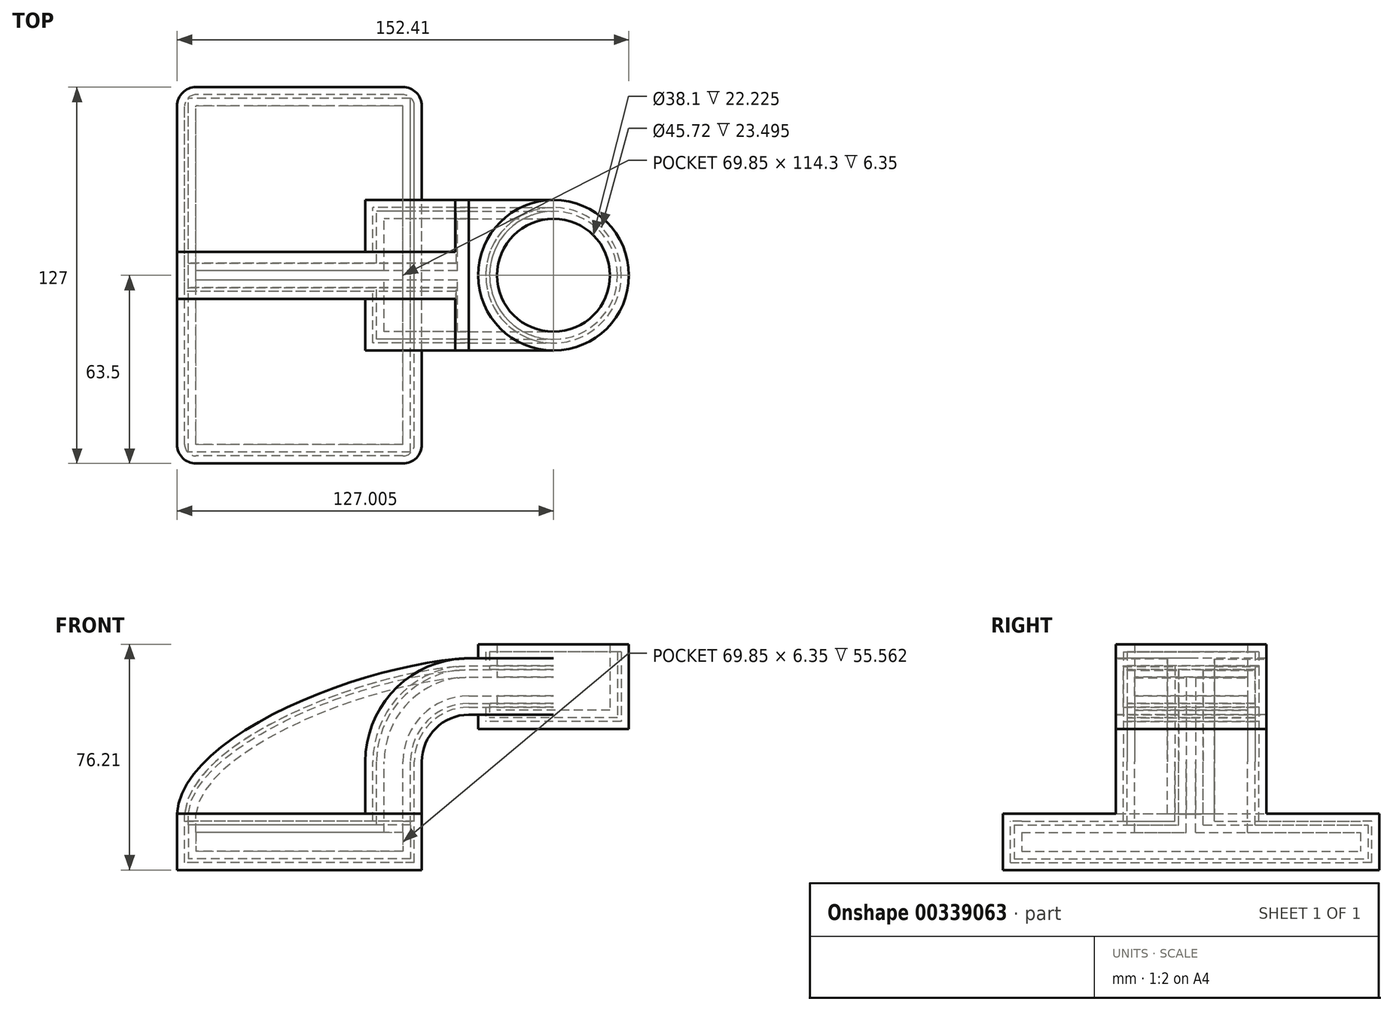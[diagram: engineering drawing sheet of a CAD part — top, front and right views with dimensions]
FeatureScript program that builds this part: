
annotation { "Feature Type Name" : "Feature", "Feature Type Description" : "" }
export const myFeature = defineFeature(function(context is Context, id is Id, definition is map)
    precondition{}
    {
        {
            var Q0;
            Q0=qCreatedBy(makeId("Front.planeOp"),FACE);
            var sketch = newSketch(context, id + "F0", { "sketchPlane" : qUnion([Q0])});
            skLineSegment(sketch, "E0.bottom", {"start": v(41.28, -9.52) * mm, "end": v(-41.28, -9.53) * mm});
            skLineSegment(sketch, "E0.top", {"start": v(41.28, 9.53) * mm, "end": v(-41.28, 9.53) * mm});
            skLineSegment(sketch, "E0.left", {"start": v(41.28, -9.52) * mm, "end": v(41.28, 9.53) * mm});
            skLineSegment(sketch, "E0.right", {"start": v(-41.28, -9.53) * mm, "end": v(-41.28, 9.53) * mm});
            skPoint(sketch, "E0.middle", {"position": v(0, 0) * mm});
            skLineSegment(sketch, "E1.bottom", {"start": v(111.13, 38.1) * mm, "end": v(60.33, 38.1) * mm});
            skLineSegment(sketch, "E1.top", {"start": v(111.13, 66.68) * mm, "end": v(60.33, 66.68) * mm});
            skLineSegment(sketch, "E1.left", {"start": v(111.13, 38.1) * mm, "end": v(111.13, 66.68) * mm});
            skLineSegment(sketch, "E1.right", {"start": v(60.33, 38.1) * mm, "end": v(60.33, 66.68) * mm});
            skPoint(sketch, "E1.middle", {"position": v(85.73, 52.39) * mm});
            skLineSegment(sketch, "E2", {"start": v(41.28, 9.53) * mm, "end": v(41.28, 27) * mm});
            skArc(sketch, "E3", {"start": v(41.27, 27) * mm, "mid": v(45.92, 38.23) * mm, "end": v(57.15, 42.88) * mm});
            skLineSegment(sketch, "E4", {"start": v(57.15, 42.88) * mm, "end": v(85.72, 42.88) * mm});
            skArc(sketch, "E5.0", {"start": v(22.23, 27) * mm, "mid": v(32.45, 51.7) * mm, "end": v(57.15, 61.93) * mm});
            skLineSegment(sketch, "E5.1", {"start": v(22.22, 9.53) * mm, "end": v(22.22, 27) * mm});
            skLineSegment(sketch, "E6", {"start": v(85.73, 38.1) * mm, "end": v(85.73, 66.68) * mm});
            skLineSegment(sketch, "E7", {"start": v(57.15, 61.93) * mm, "end": v(85.73, 61.93) * mm});
            skFitSpline(sketch, "E8", {"points": [v(-41.28, 9.52) * mm, v(57.15, 61.93) * mm], "startDerivative": vector(4.87, 81.85) * mm, "endDerivative": vector(99.43, 3.87) * mm});
            skSolve(sketch);
        }
        {
            var Q0;
            Q0=makeQuery(id+"F0.imprint","IMPRINT",FACE,{"disambiguationData":[TD([[makeQuery(id+"F0.imprint","IMPRINT",EDGE,{"derivedFrom":sQuery(id+"F0.wireOp",EDGE,"E0.bottom")}),-1.0]])]});
            extrude(context, id + "F1", {"entities" : qUnion([Q0]), "endBound" : BoundingType.SYMMETRIC, "depth" : 127 * mm});
        }
        {
            var Q0;
            {var subQ1=sQuery(id+"F0.wireOp",EDGE,"E2");Q0=makeQuery(id+"F0.imprint","IMPRINT",FACE,{"disambiguationData":[TD([[makeQuery(id+"F0.imprint","IMPRINT",EDGE,{"derivedFrom":subQ1}),1.0]])]});}
            var Q1;
            {var subQ0=sQuery(id+"F0.wireOp",EDGE,"E4");var subQ1=sQuery(id+"F0.wireOp",EDGE,"E1.right");var subQ2=makeQuery(id+"F0.imprint","INTERSECT",VERTEX,{"derivedFrom":[subQ1,subQ0]});Q1=makeQuery(id+"F0.imprint","IMPRINT",FACE,{"disambiguationData":[TD([[makeQuery(id+"F0.imprint","IMPRINT",EDGE,{"disambiguationData":[TD([[subQ2,-1.0]])],"derivedFrom":subQ1}),-1.0]])]});}
            extrude(context, id + "F2", {"entities" : qUnion([Q0, Q1]), "operationType" : NewBodyOperationType.ADD, "endBound" : BoundingType.SYMMETRIC, "depth" : 50.8 * mm});
        }
        {
            var Q0;
            {var subQ3=sQuery(id+"F0.wireOp",EDGE,"E5.1");Q0=makeQuery(id+"F0.imprint","IMPRINT",FACE,{"disambiguationData":[TD([[makeQuery(id+"F0.imprint","IMPRINT",EDGE,{"derivedFrom":subQ3}),1.0]])]});}
            extrude(context, id + "F3", {"entities" : qUnion([Q0]), "operationType" : NewBodyOperationType.ADD, "endBound" : BoundingType.SYMMETRIC, "depth" : 15.88 * mm});
        }
        {
            var Q0;
            {var subQ0=sQuery(id+"F0.wireOp",EDGE,"E1.left");Q0=makeQuery(id+"F0.imprint","IMPRINT",FACE,{"disambiguationData":[TD([[makeQuery(id+"F0.imprint","IMPRINT",EDGE,{"derivedFrom":subQ0}),1.0]])]});}
            var Q1;
            Q1=sQuery(id+"F0.wireOp",EDGE,"E6");
            revolve(context, id + "F4", {"operationType" : NewBodyOperationType.ADD, "entities" : qUnion([Q0]), "axis" : qUnion([Q1]), "revolveType" : RevolveType.FULL});
        }
        {
            var Q0;
            Q0=makeQuery(id+"F1.opExtrude","CAP_EDGE",EDGE,{"disambiguationData":[OSD([sQuery(id+"F0.wireOp",EDGE,"E0.left")])],"isStart":false});
            var Q1;
            Q1=makeQuery(id+"F1.opExtrude","CAP_EDGE",EDGE,{"disambiguationData":[OSD([sQuery(id+"F0.wireOp",EDGE,"E0.right")])],"isStart":false});
            var Q2;
            Q2=makeQuery(id+"F1.opExtrude","CAP_EDGE",EDGE,{"disambiguationData":[OSD([sQuery(id+"F0.wireOp",EDGE,"E0.left")])],"isStart":true});
            var Q3;
            Q3=makeQuery(id+"F1.opExtrude","CAP_EDGE",EDGE,{"disambiguationData":[OSD([sQuery(id+"F0.wireOp",EDGE,"E0.right")])],"isStart":true});
            fillet(context, id + "F5", {"entities" : qUnion([Q0, Q1, Q2, Q3]), "radius" : 6.35 * mm, "tangentPropagation" : true, "allowEdgeOverflow" : false});
        }
        {
            var Q0;
            Q0=makeQuery(id+"F4.opRevolve","SWEPT_FACE",FACE,{"disambiguationData":[OSD([sQuery(id+"F0.wireOp",EDGE,"E1.top")])]});
            shell(context, id + "F6", {"entities" : qUnion([Q0]), "thickness" : 6.35 * mm});
        }
        {
            var Q0;
            Q0=makeQuery(id+"F3.opExtrude","CAP_FACE",FACE,{"disambiguationData":[OSD([sQuery(id+"F0.wireOp",EDGE,"E0.top"),sQuery(id+"F0.wireOp",EDGE,"E5.0"),sQuery(id+"F0.wireOp",EDGE,"E5.1"),sQuery(id+"F0.wireOp",EDGE,"E8")])],"isStart":true});
            shell(context, id + "F7", {"entities" : qUnion([Q0]), "thickness" : 2.54 * mm});
        }
    });
